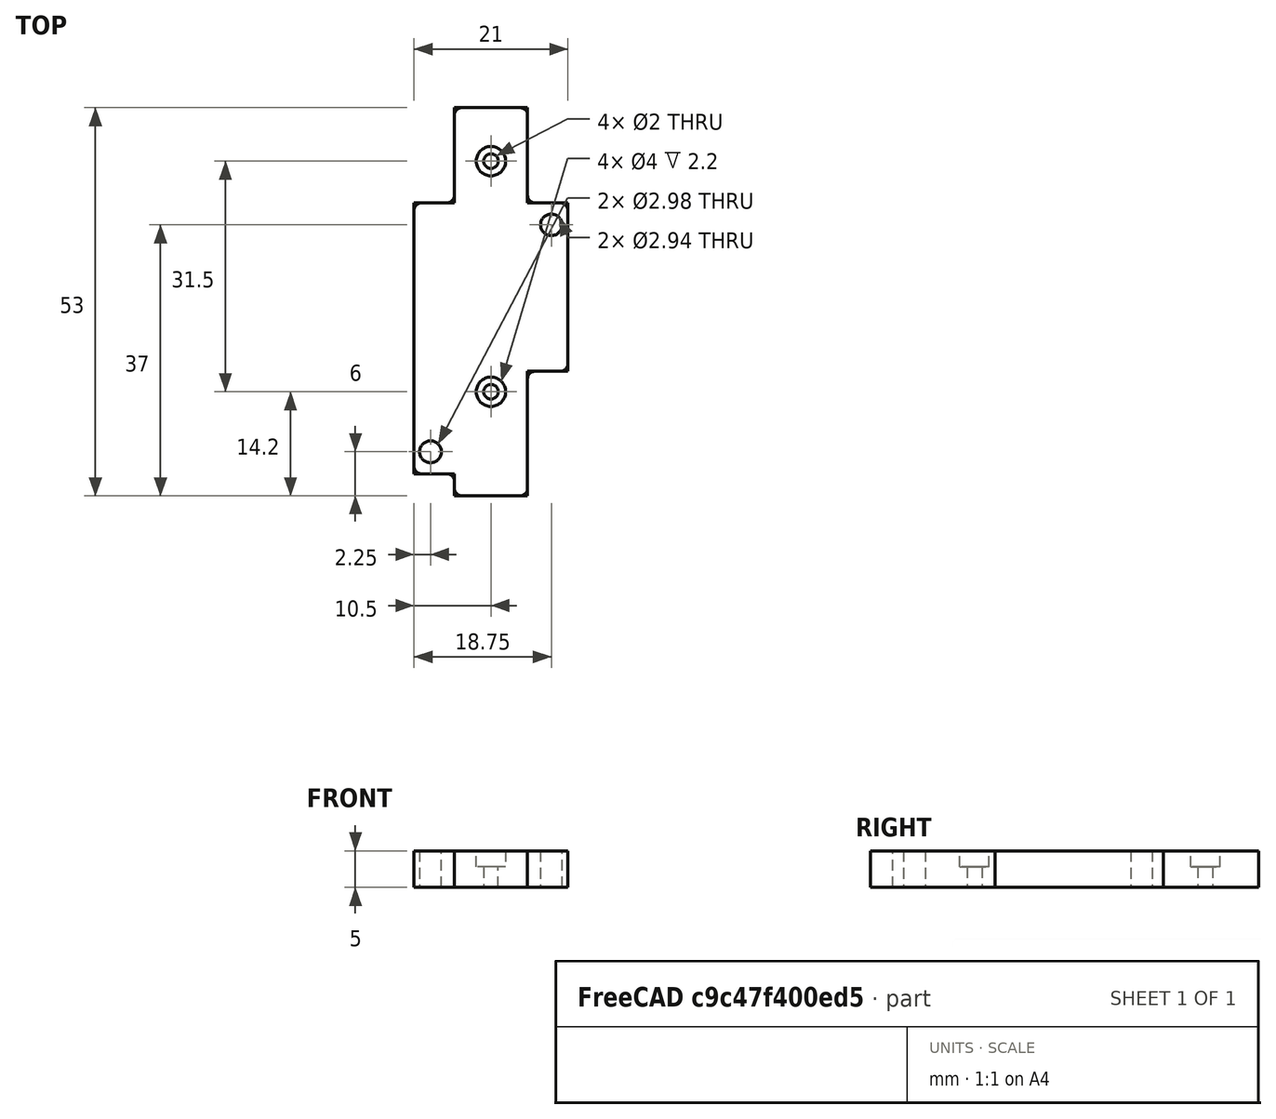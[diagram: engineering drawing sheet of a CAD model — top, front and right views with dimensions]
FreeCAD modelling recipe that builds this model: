
FCSTD DOCUMENT  (FreeCAD 0.19R24291 (Git))
Label: LM2596 Din Rail Mount
License: All rights reserved
LicenseURL: http://en.wikipedia.org/wiki/All_rights_reserved
objects: Sketcher::SketchObject×2, Mesh::Feature×1, PartDesign::Pad×1, PartDesign::Pocket×1, PartDesign::Body×1, Part::Fillet×1
note: 8 computed .brp shape members not serialized (recipe doc carries the construction recipe); baked Part::Feature solids carry a one-line shape summary decoded from their .brp

FEATURE [Mesh::Feature] pcb_din_clip_x3
  Placement = pos=(5,-150,-159) rot=(0,1,0;4.71239rad)
FEATURE [Sketcher::SketchObject] Sketch
  FullyConstrained = false
  MapMode = 5
  Support = -> [XY_Plane]
  sketch-geometry (22):
    g0: LineSegment StartX=-10.5 StartY=21.5 StartZ=0 EndX=10.5 EndY=21.5 EndZ=0
    g1: LineSegment StartX=10.5 StartY=21.5 StartZ=0 EndX=10.5 EndY=-21.5 EndZ=0
    g2: LineSegment StartX=10.5 StartY=-21.5 StartZ=0 EndX=-10.5 EndY=-21.5 EndZ=0
    g3: LineSegment StartX=-10.5 StartY=-21.5 StartZ=0 EndX=-10.5 EndY=21.5 EndZ=0
    g4: Circle CenterX=8.25 CenterY=15.5 CenterZ=0 NormalX=0 NormalY=0 NormalZ=1 AngleXU=0 Radius=1.5
    g5: Circle CenterX=-8.25 CenterY=-15.5 CenterZ=0 NormalX=0 NormalY=0 NormalZ=1 AngleXU=0 Radius=1.5
    g6: LineSegment StartX=-10.5 StartY=-18.5 StartZ=0 EndX=-5 EndY=-18.5 EndZ=0
    g7: LineSegment StartX=-5 StartY=-18.5 StartZ=0 EndX=-5 EndY=-21.5 EndZ=0
    g8: LineSegment StartX=-5 StartY=-21.5 StartZ=0 EndX=5 EndY=-21.5 EndZ=0
    g9: LineSegment StartX=5 StartY=-21.5 StartZ=0 EndX=5 EndY=-4.5 EndZ=0
    g10: LineSegment StartX=5 StartY=-4.5 StartZ=0 EndX=10.5 EndY=-4.5 EndZ=0
    g11: LineSegment StartX=10.5 StartY=-4.5 StartZ=0 EndX=10.5 EndY=18.5 EndZ=0
    g12: LineSegment StartX=10.5 StartY=18.5 StartZ=0 EndX=5 EndY=18.5 EndZ=0
    g13: LineSegment StartX=5 StartY=31.5 StartZ=0 EndX=-5 EndY=31.5 EndZ=0
    g14: LineSegment StartX=-10.5 StartY=18.5 StartZ=0 EndX=-10.5 EndY=-18.5 EndZ=0
    g15: LineSegment StartX=5 StartY=18.5 StartZ=0 EndX=5 EndY=31.5 EndZ=0
    g16: LineSegment StartX=-10.5 StartY=18.5 StartZ=0 EndX=-5 EndY=18.5 EndZ=0
    g17: LineSegment StartX=-5 StartY=18.5 StartZ=0 EndX=-5 EndY=31.5 EndZ=0
    g18: Circle CenterX=-8.25 CenterY=-15.5 CenterZ=0 NormalX=0 NormalY=0 NormalZ=1 AngleXU=0 Radius=1.48896
    g19: Circle CenterX=8.25 CenterY=15.5 CenterZ=0 NormalX=0 NormalY=0 NormalZ=1 AngleXU=0 Radius=1.47209
    g20: Circle CenterX=0 CenterY=-7.3 CenterZ=0 NormalX=0 NormalY=0 NormalZ=1 AngleXU=0 Radius=1
    g21: Circle CenterX=0 CenterY=24.2 CenterZ=0 NormalX=0 NormalY=0 NormalZ=1 AngleXU=0 Radius=1
  constraints (60):
    c: Coincident(g0,g1)
    c: Coincident(g1,g2)
    c: Coincident(g2,g3)
    c: Coincident(g3,g0)
    c: Horizontal(g0)
    c: Horizontal(g2)
    c: Vertical(g1)
    c: Vertical(g3)
    c: DistanceX(g0,g0) = 21
    c: DistanceY(g3,g3) = 43
    c: Symmetric(g2,g0,g-1)
    c: Radius(g4) = 1.5
    c: Equal(g4,g5)
    c: DistanceY(g5,g4) = 31
    c: Symmetric(g4,g5,g-1)
    c: PointOnObject(g6,g3)
    c: Horizontal(g6)
    c: Coincident(g6,g7)
    c: PointOnObject(g7,g2)
    c: Vertical(g7)
    c: Coincident(g7,g8)
    c: PointOnObject(g8,g2)
    c: Coincident(g8,g9)
    c: Coincident(g9,g10)
    c: PointOnObject(g10,g1)
    c: Horizontal(g10)
    c: Coincident(g10,g11)
    c: PointOnObject(g11,g1)
    c: Coincident(g11,g12)
    c: Horizontal(g12)
    c: Horizontal(g13)
    c: PointOnObject(g14,g3)
    c: Coincident(g14,g6)
    c: Equal(g6,g10)
    c: Equal(g10,g12)
    c: Vertical(g9)
    c: DistanceX(g8,g8) = 10
    c: Coincident(g15,g12)
    c: Coincident(g15,g13)
    c: Vertical(g15)
    c: Coincident(g14,g16)
    c: Horizontal(g16)
    c: Coincident(g16,g17)
    c: Coincident(g17,g13)
    c: Vertical(g17)
    c: Equal(g8,g13)
    c: DistanceY(g14,g0) = 3
    c: Horizontal(g16,g12)
    c: DistanceY(g17,g17) = 13
    c: DistanceX(g5,g4) = 16.5
    c: DistanceY(g7,g7) = 3
    c: DistanceY(g9,g9) = 17
    c: Coincident(g18,g5)
    c: Coincident(g19,g4)
    c: PointOnObject(g20,g-2)
    c: PointOnObject(g21,g-2)
    c: Radius(g21) = 1
    c: Radius(g20) = 1
    c: DistanceY(g20,g-1) = 7.3
    c: DistanceY(g-1,g21) = 24.2
FEATURE [PartDesign::Pad] Pad
  Direction = (1,1,1)
  Length = 5
  Length2 = 100
  Profile = -> Sketch
  Type = 0
FEATURE [Sketcher::SketchObject] Sketch001
  ExternalGeometry = -> [Pad]
  FullyConstrained = true
  MapMode = 5
  Placement = pos=(0,0,5) rot=(0,0,1;0rad)
  Support = -> [Pad]
  sketch-geometry (2):
    g0: Circle CenterX=0 CenterY=24.2 CenterZ=0 NormalX=0 NormalY=0 NormalZ=1 AngleXU=0 Radius=2
    g1: Circle CenterX=0 CenterY=-7.3 CenterZ=0 NormalX=0 NormalY=0 NormalZ=1 AngleXU=0 Radius=2
  constraints (4):
    c: Coincident(g0,g-3)
    c: Coincident(g1,g-4)
    c: Radius(g0) = 2
    c: Equal(g0,g1)
FEATURE [PartDesign::Pocket] Pocket
  BaseFeature = -> Pad
  Length = 2.2
  Length2 = 100
  Profile = -> Sketch001
  Type = 0
FEATURE [PartDesign::Body] Body
  Group = -> [Sketch,Pad,Sketch001,Pocket]
  Origin = -> Origin
  Tip = -> Pocket
FEATURE [Part::Fillet] Fillet
  Base = -> Pocket
  Edges = 12 edges r=1: [Edge1,Edge2,Edge5,Edge8,Edge37,Edge38,Edge39,Edge40,Edge41,Edge42,Edge43,Edge44]
